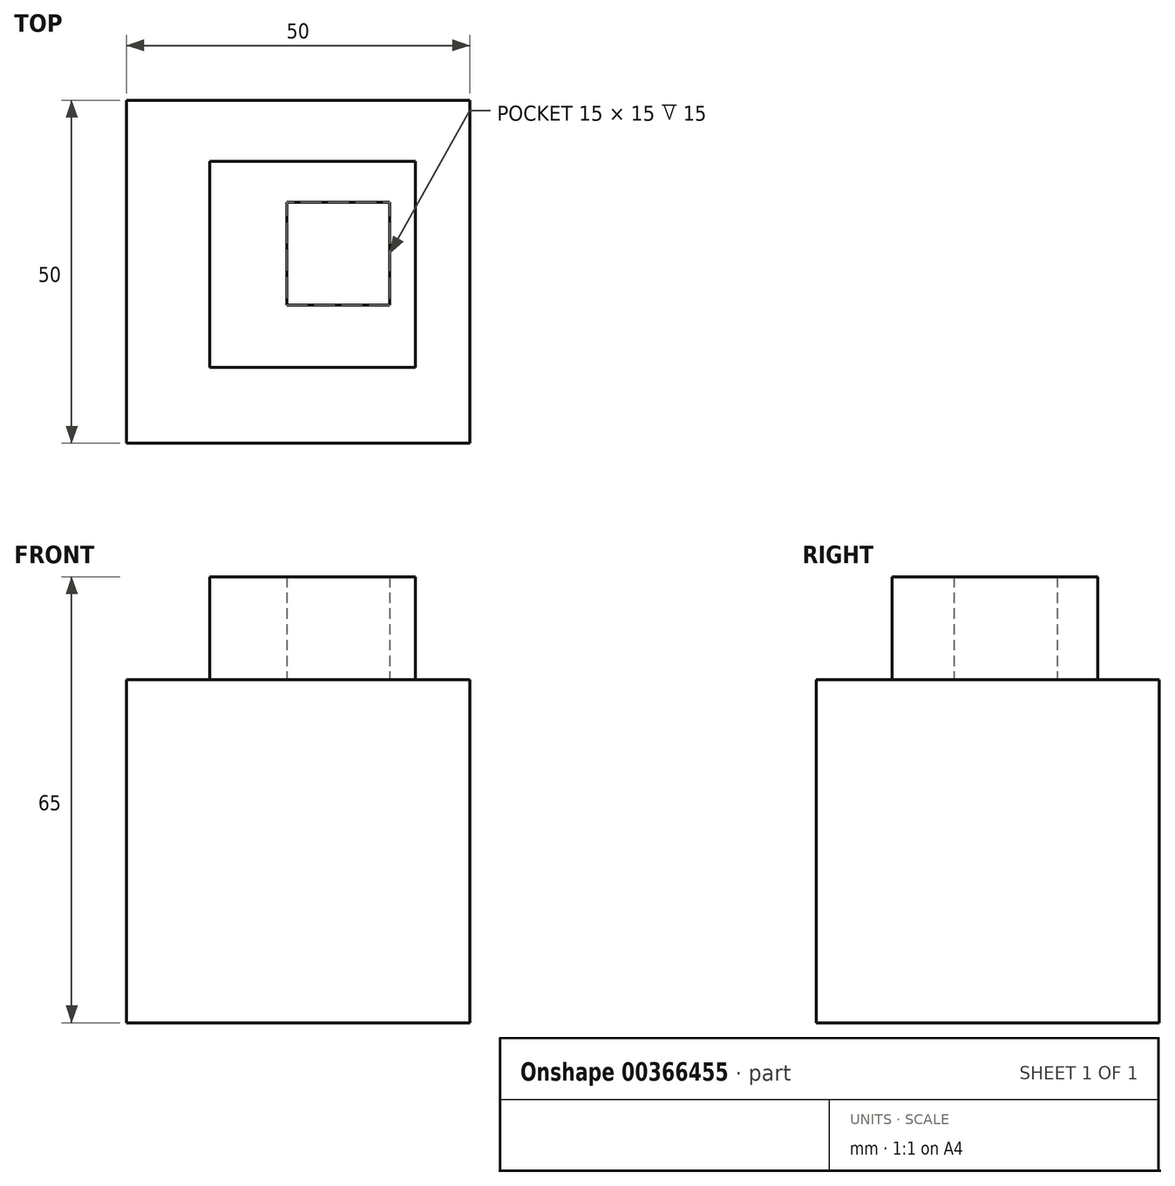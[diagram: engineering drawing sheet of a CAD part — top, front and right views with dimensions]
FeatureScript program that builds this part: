
annotation { "Feature Type Name" : "Feature", "Feature Type Description" : "" }
export const myFeature = defineFeature(function(context is Context, id is Id, definition is map)
    precondition{}
    {
        {
            var Q0;
            Q0=qCreatedBy(makeId("Top.planeOp"),FACE);
            var sketch = newSketch(context, id + "F0", { "sketchPlane" : qUnion([Q0])});
            skLineSegment(sketch, "E0.bottom", {"start": v(0, 0) * mm, "end": v(-50, 0) * mm});
            skLineSegment(sketch, "E0.top", {"start": v(0, 50) * mm, "end": v(-50, 50) * mm});
            skLineSegment(sketch, "E0.left", {"start": v(0, 0) * mm, "end": v(0, 50) * mm});
            skLineSegment(sketch, "E0.right", {"start": v(-50, 0) * mm, "end": v(-50, 50) * mm});
            skSolve(sketch);
        }
        {
            var Q0;
            Q0=makeQuery(id+"F0.imprint","IMPRINT",FACE,{"disambiguationData":[TD([[makeQuery(id+"F0.imprint","IMPRINT",EDGE,{"derivedFrom":sQuery(id+"F0.wireOp",EDGE,"E0.bottom")}),-1.0]])]});
            extrude(context, id + "F1", {"entities" : qUnion([Q0]), "depth" : 50 * mm});
        }
        {
            var Q0;
            Q0=makeQuery(id+"F1.opExtrude","CAP_FACE",FACE,{"disambiguationData":[OSD([sQuery(id+"F0.wireOp",EDGE,"E0.bottom"),sQuery(id+"F0.wireOp",EDGE,"E0.top"),sQuery(id+"F0.wireOp",EDGE,"E0.left"),sQuery(id+"F0.wireOp",EDGE,"E0.right")])],"isStart":false});
            var sketch = newSketch(context, id + "F2", { "sketchPlane" : qUnion([Q0])});
            skLineSegment(sketch, "E1.bottom", {"start": v(-37.9, 41.07) * mm, "end": v(-7.9, 41.07) * mm});
            skLineSegment(sketch, "E1.top", {"start": v(-37.9, 11.07) * mm, "end": v(-7.9, 11.07) * mm});
            skLineSegment(sketch, "E1.left", {"start": v(-37.9, 41.07) * mm, "end": v(-37.9, 11.07) * mm});
            skLineSegment(sketch, "E1.right", {"start": v(-7.9, 41.07) * mm, "end": v(-7.9, 11.07) * mm});
            skLineSegment(sketch, "E2.bottom", {"start": v(-26.63, 35.12) * mm, "end": v(-11.63, 35.12) * mm});
            skLineSegment(sketch, "E2.top", {"start": v(-26.63, 20.12) * mm, "end": v(-11.63, 20.12) * mm});
            skLineSegment(sketch, "E2.left", {"start": v(-26.63, 35.12) * mm, "end": v(-26.63, 20.12) * mm});
            skLineSegment(sketch, "E2.right", {"start": v(-11.63, 35.12) * mm, "end": v(-11.63, 20.12) * mm});
            skSolve(sketch);
        }
        {
            var Q0;
            Q0 = qSketchRegion(id + "F2", true);
            extrude(context, id + "F3", {"entities" : qUnion([Q0]), "operationType" : NewBodyOperationType.ADD, "depth" : 15 * mm});
        }
        {
            var Q0;
            Q0 = qSketchRegion(id + "F2", true);
            extrude(context, id + "F4", {"entities" : qUnion([Q0]), "operationType" : NewBodyOperationType.ADD, "depth" : 15 * mm});
        }
    });
